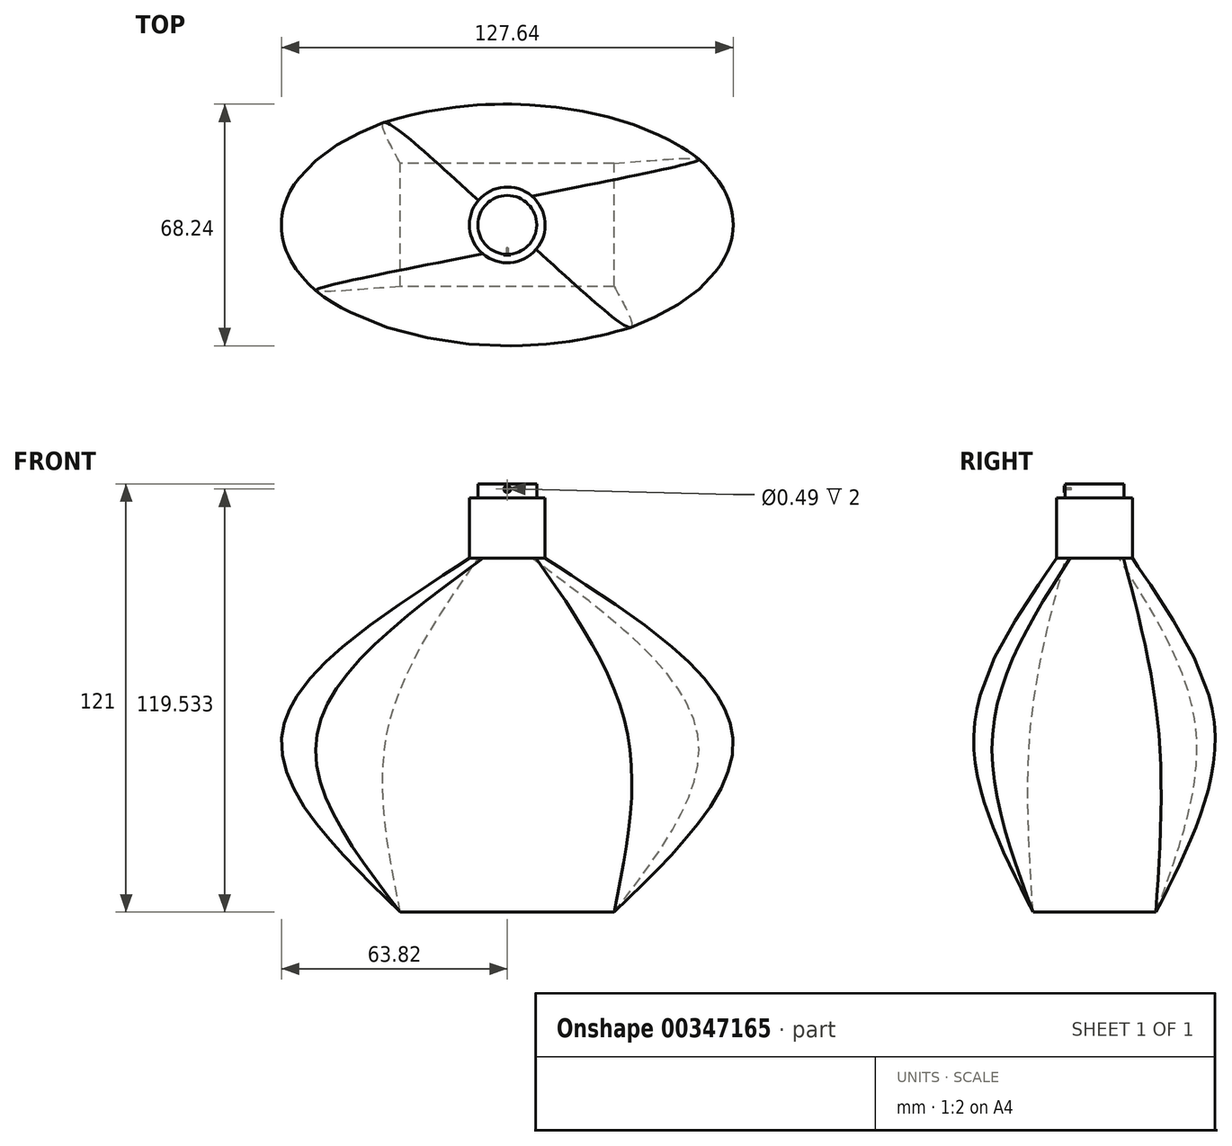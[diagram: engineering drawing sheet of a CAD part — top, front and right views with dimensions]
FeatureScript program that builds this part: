
annotation { "Feature Type Name" : "Feature", "Feature Type Description" : "" }
export const myFeature = defineFeature(function(context is Context, id is Id, definition is map)
    precondition{}
    {
        {
            var Q0;
            Q0=qCreatedBy(makeId("Top.planeOp"),FACE);
            cPlane(context, id + "F0", {"entities" : qUnion([Q0]), "cplaneType" : CPlaneType.OFFSET, "offset" : 50 * mm, "width" : 150 * mm, "height" : 150 * mm});
        }
        {
            var Q0;
            Q0=qCreatedBy(makeId("Top.planeOp"),FACE);
            var sketch = newSketch(context, id + "F1", { "sketchPlane" : qUnion([Q0])});
            skLineSegment(sketch, "E0.bottom", {"start": v(30.17, -17.37) * mm, "end": v(-30.17, -17.37) * mm});
            skLineSegment(sketch, "E0.top", {"start": v(30.17, 17.37) * mm, "end": v(-30.17, 17.37) * mm});
            skLineSegment(sketch, "E0.left", {"start": v(30.17, -17.37) * mm, "end": v(30.17, 17.37) * mm});
            skLineSegment(sketch, "E0.right", {"start": v(-30.17, -17.37) * mm, "end": v(-30.17, 17.37) * mm});
            skPoint(sketch, "E0.middle", {"position": v(0, 0) * mm});
            skSolve(sketch);
        }
        {
            var Q0;
            Q0=qCreatedBy(id+"F0.planeOp",FACE);
            var sketch = newSketch(context, id + "F2", { "sketchPlane" : qUnion([Q0])});
            skEllipse(sketch, "E1", {"center": v(0, 0) * mm, "majorRadius": 63.69 * mm, "minorRadius": 34.1 * mm, "majorAxis": v(1, 0)});
            skSolve(sketch);
        }
        {
            var Q0;
            Q0=qCreatedBy(id+"F0.planeOp",FACE);
            cPlane(context, id + "F3", {"entities" : qUnion([Q0]), "cplaneType" : CPlaneType.OFFSET, "offset" : 50 * mm, "width" : 150 * mm, "height" : 150 * mm});
        }
        {
            var Q0;
            Q0=qCreatedBy(id+"F3.planeOp",FACE);
            var sketch = newSketch(context, id + "F4", { "sketchPlane" : qUnion([Q0])});
            skCircle(sketch, "E2", {"center": v(0, 0) * mm, "radius": 10.7 * mm});
            skSolve(sketch);
        }
        {
            var Q0;
            Q0=makeQuery(id+"F1.imprint","IMPRINT",FACE,{"disambiguationData":[TD([[makeQuery(id+"F1.imprint","IMPRINT",EDGE,{"derivedFrom":sQuery(id+"F1.wireOp",EDGE,"E0.bottom")}),-1.0]])]});
            var Q1;
            Q1=makeQuery(id+"F2.imprint","IMPRINT",FACE,{"disambiguationData":[TD([[makeQuery(id+"F2.imprint","IMPRINT",EDGE,{"derivedFrom":sQuery(id+"F2.wireOp",EDGE,"E1")}),1.0]])]});
            var Q2;
            Q2=makeQuery(id+"F4.imprint","IMPRINT",FACE,{"disambiguationData":[TD([[makeQuery(id+"F4.imprint","IMPRINT",EDGE,{"derivedFrom":sQuery(id+"F4.wireOp",EDGE,"E2")}),1.0]])]});
            loft(context, id + "F5", {"sheetProfilesArray" : [{ "sheetProfileEntities" : qUnion([Q0]) }, { "sheetProfileEntities" : qUnion([Q1]) }, { "sheetProfileEntities" : qUnion([Q2]) }]});
        }
        {
            var Q0;
            Q0=makeQuery(id+"F5.opLoft","CAP_FACE",FACE,{"disambiguationData":[OSD([makeQuery(id+"F4.imprint","IMPRINT",FACE,{"disambiguationData":[TD([[makeQuery(id+"F4.imprint","IMPRINT",EDGE,{"derivedFrom":sQuery(id+"F4.wireOp",EDGE,"E2")}),1.0]])]})])],"isStart":true});
            extrude(context, id + "F6", {"entities" : qUnion([Q0]), "operationType" : NewBodyOperationType.ADD, "depth" : 17 * mm});
        }
        {
            var Q0;
            Q0=makeQuery(id+"F6.opExtrude","CAP_FACE",FACE,{"disambiguationData":[OSD([makeQuery(id+"F4.imprint","IMPRINT",FACE,{"disambiguationData":[TD([[makeQuery(id+"F4.imprint","IMPRINT",EDGE,{"derivedFrom":sQuery(id+"F4.wireOp",EDGE,"E2")}),1.0]])]})])],"isStart":false});
            var sketch = newSketch(context, id + "F7", { "sketchPlane" : qUnion([Q0])});
            skCircle(sketch, "E3", {"center": v(0, 0) * mm, "radius": 8.32 * mm});
            skSolve(sketch);
        }
        {
            var Q0;
            Q0=makeQuery(id+"F7.imprint","IMPRINT",FACE,{"disambiguationData":[TD([[makeQuery(id+"F7.imprint","IMPRINT",EDGE,{"derivedFrom":sQuery(id+"F7.wireOp",EDGE,"E3")}),1.0]])]});
            extrude(context, id + "F8", {"entities" : qUnion([Q0]), "operationType" : NewBodyOperationType.ADD, "depth" : 4 * mm});
        }
        {
            var Q0;
            Q0=qCreatedBy(makeId("Front.planeOp"),FACE);
            var sketch = newSketch(context, id + "F9", { "sketchPlane" : qUnion([Q0])});
            skCircle(sketch, "E4", {"center": v(0, 119.5) * mm, "radius": 0.97 * mm});
            skSolve(sketch);
        }
        {
            var Q0;
            Q0=qSketchRegion(id+"F9",true);
            extrude(context, id + "F10", {"entities" : qUnion([Q0]), "operationType" : NewBodyOperationType.ADD, "depth" : 8.5 * mm});
        }
        {
            var Q0;
            Q0=makeQuery(id+"F10.opExtrude","CAP_FACE",FACE,{"disambiguationData":[OSD([sQuery(id+"F9.wireOp",EDGE,"E4")])],"isStart":false});
            var sketch = newSketch(context, id + "F11", { "sketchPlane" : qUnion([Q0])});
            skSolve(sketch);
        }
        {
            var Q0;
            Q0=makeQuery(id+"F11.imprint","IMPRINT",FACE,{"disambiguationData":[TD([[makeQuery(id+"F11.imprint","IMPRINT",EDGE,{"derivedFrom":makeQuery(id+"F10.opExtrude","CAP_EDGE",EDGE,{"disambiguationData":[OSD([sQuery(id+"F9.wireOp",EDGE,"E4")])],"isStart":false})}),1.0]])]});
            var sketch = newSketch(context, id + "F12", { "sketchPlane" : qUnion([Q0])});
            skCircle(sketch, "E5", {"center": v(0, 119.53) * mm, "radius": 0.25 * mm});
            skSolve(sketch);
        }
        {
            var Q0;
            Q0=qSketchRegion(id+"F12",true);
            extrude(context, id + "F13", {"entities" : qUnion([Q0]), "operationType" : NewBodyOperationType.REMOVE, "oppositeDirection" : true, "depth" : 2 * mm});
        }
        {
            var Q0;
            Q0=qCreatedBy(makeId("Front.planeOp"),FACE);
            var sketch = newSketch(context, id + "F14", { "sketchPlane" : qUnion([Q0])});
            skCircle(sketch, "E6", {"center": v(0, 119.52) * mm, "radius": 0.07 * mm});
            skSolve(sketch);
        }
        {
            var Q0;
            Q0=qSketchRegion(id+"F14",true);
            extrude(context, id + "F15", {"entities" : qUnion([Q0]), "operationType" : NewBodyOperationType.ADD, "depth" : 8.5 * mm});
        }
    });
